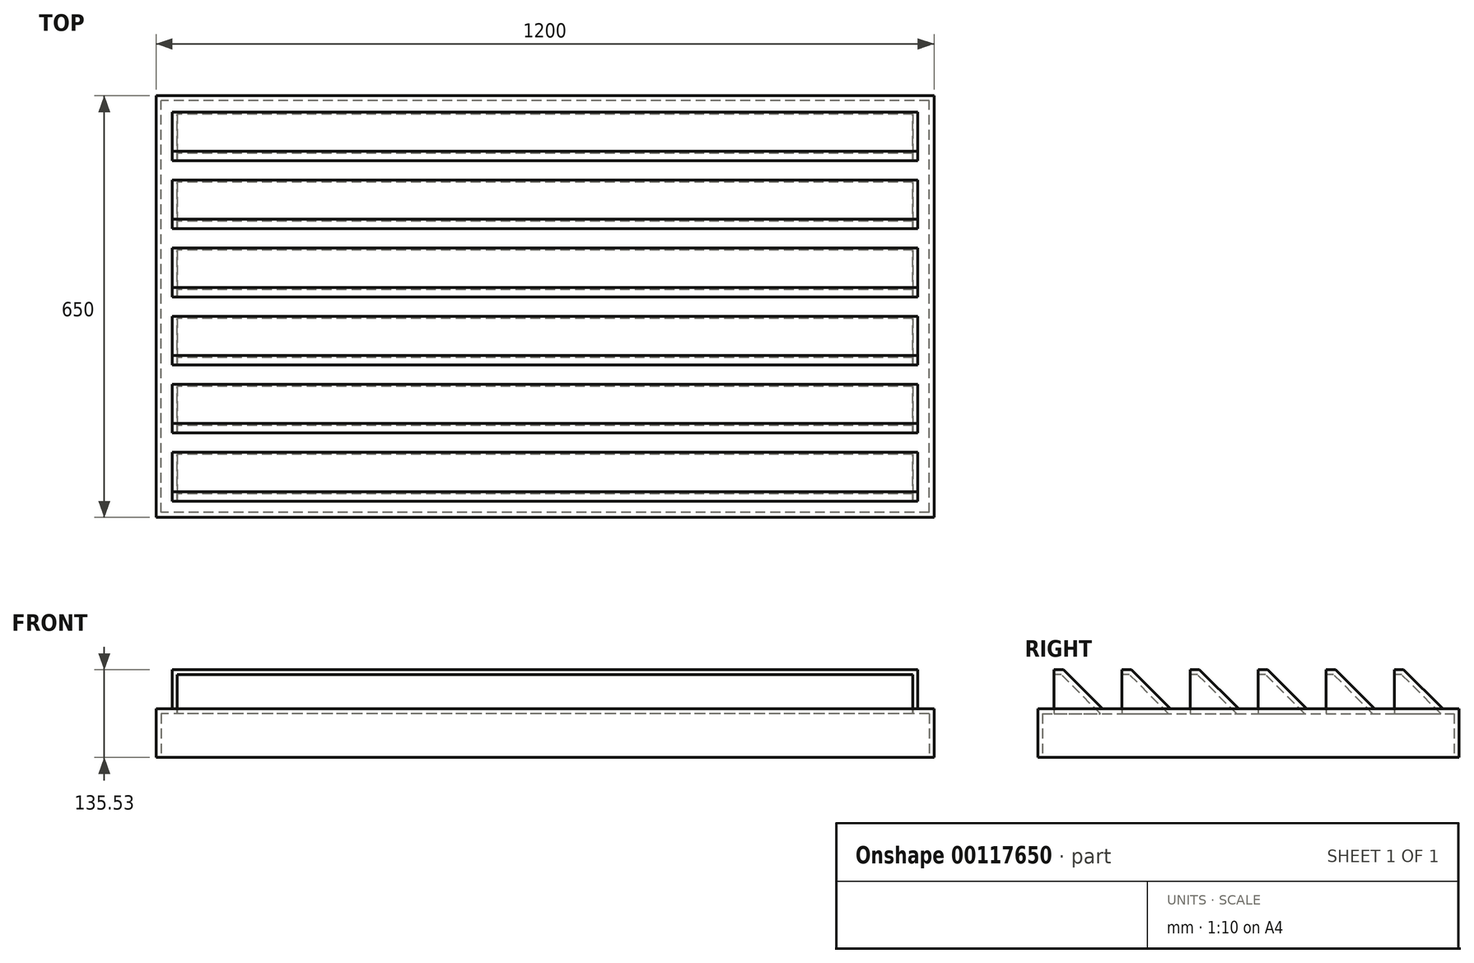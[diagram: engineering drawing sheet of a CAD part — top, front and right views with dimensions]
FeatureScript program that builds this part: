
annotation { "Feature Type Name" : "Feature", "Feature Type Description" : "" }
export const myFeature = defineFeature(function(context is Context, id is Id, definition is map)
    precondition{}
    {
        {
            var Q0;
            Q0=qCreatedBy(makeId("Top.planeOp"),FACE);
            var sketch = newSketch(context, id + "F0", { "sketchPlane" : qUnion([Q0])});
            skLineSegment(sketch, "E0.bottom", {"start": v(600, -325) * mm, "end": v(-600, -325) * mm});
            skLineSegment(sketch, "E0.top", {"start": v(600, 325) * mm, "end": v(-600, 325) * mm});
            skLineSegment(sketch, "E0.left", {"start": v(600, -325) * mm, "end": v(600, 325) * mm});
            skLineSegment(sketch, "E0.right", {"start": v(-600, -325) * mm, "end": v(-600, 325) * mm});
            skPoint(sketch, "E0.middle", {"position": v(0, 0) * mm});
            skSolve(sketch);
        }
        {
            var Q0;
            Q0=makeQuery(id+"F0.imprint","IMPRINT",FACE,{"disambiguationData":[TD([[makeQuery(id+"F0.imprint","IMPRINT",EDGE,{"derivedFrom":sQuery(id+"F0.wireOp",EDGE,"E0.bottom")}),-1.0]])]});
            extrude(context, id + "F1", {"entities" : qUnion([Q0]), "depth" : 75 * mm});
        }
        {
            var Q0;
            Q0=makeQuery(id+"F1.opExtrude","SWEPT_FACE",FACE,{"disambiguationData":[OSD([sQuery(id+"F0.wireOp",EDGE,"E0.right")])]});
            var sketch = newSketch(context, id + "F2", { "sketchPlane" : qUnion([Q0])});
            skLineSegment(sketch, "E1", {"start": v(-300, 75) * mm, "end": v(-225, 150) * mm});
            skLineSegment(sketch, "E2", {"start": v(-225, 150) * mm, "end": v(-225, 75) * mm});
            skLineSegment(sketch, "E3", {"start": v(-239.47, 135.53) * mm, "end": v(360, 135.53) * mm});
            skLineSegment(sketch, "E4.1.0.0", {"start": v(-195, 75) * mm, "end": v(-120, 150) * mm});
            skLineSegment(sketch, "E4.1.0.1", {"start": v(-120, 150) * mm, "end": v(-120, 75) * mm});
            skLineSegment(sketch, "E4.2.0.0", {"start": v(-90, 75) * mm, "end": v(-15, 150) * mm});
            skLineSegment(sketch, "E4.2.0.1", {"start": v(-15, 150) * mm, "end": v(-15, 75) * mm});
            skLineSegment(sketch, "E4.3.0.0", {"start": v(15, 75) * mm, "end": v(90, 150) * mm});
            skLineSegment(sketch, "E4.3.0.1", {"start": v(90, 150) * mm, "end": v(90, 75) * mm});
            skLineSegment(sketch, "E4.4.0.0", {"start": v(120, 75) * mm, "end": v(195, 150) * mm});
            skLineSegment(sketch, "E4.4.0.1", {"start": v(195, 150) * mm, "end": v(195, 75) * mm});
            skLineSegment(sketch, "E4.5.0.0", {"start": v(225, 75) * mm, "end": v(300, 150) * mm});
            skLineSegment(sketch, "E4.5.0.1", {"start": v(300, 150) * mm, "end": v(300, 75) * mm});
            skLineSegment(sketch, "E4.direction1", {"start": v(-300, 75) * mm, "end": v(-195, 75) * mm, "construction": true});
            skSolve(sketch);
        }
        {
            var Q0;
            {var subQ0=sQuery(id+"F2.wireOp",EDGE,"E1");var subQ1=makeQuery(id+"F1.opExtrude","CAP_EDGE",EDGE,{"disambiguationData":[OSD([sQuery(id+"F0.wireOp",EDGE,"E0.right")])],"isStart":false});var subQ2=makeQuery(id+"F2.imprint","INTERSECT",VERTEX,{"derivedFrom":[subQ1,subQ0]});Q0=makeQuery(id+"F2.imprint","IMPRINT",FACE,{"disambiguationData":[TD([[makeQuery(id+"F2.imprint","IMPRINT",EDGE,{"disambiguationData":[TD([[subQ2,-1.0]])],"derivedFrom":subQ0}),-1.0]])]});}
            var Q1;
            {var subQ0=sQuery(id+"F2.wireOp",EDGE,"E4.1.0.0");var subQ1=sQuery(id+"F2.wireOp",EDGE,"E3");var subQ2=makeQuery(id+"F2.imprint","INTERSECT",VERTEX,{"derivedFrom":[subQ1,subQ0]});Q1=makeQuery(id+"F2.imprint","IMPRINT",FACE,{"disambiguationData":[TD([[makeQuery(id+"F2.imprint","IMPRINT",EDGE,{"disambiguationData":[TD([[subQ2,-1.0]])],"derivedFrom":subQ1}),-1.0]])]});}
            var Q2;
            {var subQ0=sQuery(id+"F2.wireOp",EDGE,"E4.2.0.0");var subQ1=sQuery(id+"F2.wireOp",EDGE,"E3");var subQ2=makeQuery(id+"F2.imprint","INTERSECT",VERTEX,{"derivedFrom":[subQ1,subQ0]});Q2=makeQuery(id+"F2.imprint","IMPRINT",FACE,{"disambiguationData":[TD([[makeQuery(id+"F2.imprint","IMPRINT",EDGE,{"disambiguationData":[TD([[subQ2,-1.0]])],"derivedFrom":subQ1}),-1.0]])]});}
            var Q3;
            {var subQ0=sQuery(id+"F2.wireOp",EDGE,"E4.3.0.0");var subQ1=sQuery(id+"F2.wireOp",EDGE,"E3");var subQ2=makeQuery(id+"F2.imprint","INTERSECT",VERTEX,{"derivedFrom":[subQ1,subQ0]});Q3=makeQuery(id+"F2.imprint","IMPRINT",FACE,{"disambiguationData":[TD([[makeQuery(id+"F2.imprint","IMPRINT",EDGE,{"disambiguationData":[TD([[subQ2,-1.0]])],"derivedFrom":subQ1}),-1.0]])]});}
            var Q4;
            {var subQ0=sQuery(id+"F2.wireOp",EDGE,"E4.4.0.0");var subQ1=sQuery(id+"F2.wireOp",EDGE,"E3");var subQ2=makeQuery(id+"F2.imprint","INTERSECT",VERTEX,{"derivedFrom":[subQ1,subQ0]});Q4=makeQuery(id+"F2.imprint","IMPRINT",FACE,{"disambiguationData":[TD([[makeQuery(id+"F2.imprint","IMPRINT",EDGE,{"disambiguationData":[TD([[subQ2,-1.0]])],"derivedFrom":subQ1}),-1.0]])]});}
            var Q5;
            {var subQ0=sQuery(id+"F2.wireOp",EDGE,"E4.5.0.1");var subQ1=sQuery(id+"F2.wireOp",EDGE,"E3");var subQ2=makeQuery(id+"F2.imprint","INTERSECT",VERTEX,{"derivedFrom":[subQ1,subQ0]});Q5=makeQuery(id+"F2.imprint","IMPRINT",FACE,{"disambiguationData":[TD([[makeQuery(id+"F2.imprint","IMPRINT",EDGE,{"disambiguationData":[TD([[subQ2,1.0]])],"derivedFrom":subQ1}),-1.0]])]});}
            extrude(context, id + "F3", {"entities" : qUnion([Q0, Q1, Q2, Q3, Q4, Q5]), "operationType" : NewBodyOperationType.ADD, "oppositeDirection" : true, "depth" : 1175 * mm, "hasSecondDirection" : true, "secondDirectionOppositeDirection" : true, "secondDirectionDepth" : 25 * mm});
        }
        {
            var Q0;
            Q0=makeQuery(id+"F3.opExtrude","SWEPT_FACE",FACE,{"disambiguationData":[OSD([sQuery(id+"F2.wireOp",EDGE,"E2")])]});
            var Q1;
            Q1=makeQuery(id+"F3.opExtrude","SWEPT_FACE",FACE,{"disambiguationData":[OSD([sQuery(id+"F2.wireOp",EDGE,"475c7ac5-b6c0-4911-8d2d-dd895b44ecf6.1.0.1")])]});
            var Q2;
            Q2=makeQuery(id+"F3.opExtrude","SWEPT_FACE",FACE,{"disambiguationData":[OSD([sQuery(id+"F2.wireOp",EDGE,"475c7ac5-b6c0-4911-8d2d-dd895b44ecf6.2.0.1")])]});
            var Q3;
            Q3=makeQuery(id+"F3.opExtrude","SWEPT_FACE",FACE,{"disambiguationData":[OSD([sQuery(id+"F2.wireOp",EDGE,"475c7ac5-b6c0-4911-8d2d-dd895b44ecf6.3.0.1")])]});
            var Q4;
            Q4=makeQuery(id+"F3.opExtrude","SWEPT_FACE",FACE,{"disambiguationData":[OSD([sQuery(id+"F2.wireOp",EDGE,"475c7ac5-b6c0-4911-8d2d-dd895b44ecf6.4.0.1")])]});
            var Q5;
            Q5=makeQuery(id+"F3.opExtrude","SWEPT_FACE",FACE,{"disambiguationData":[OSD([sQuery(id+"F2.wireOp",EDGE,"475c7ac5-b6c0-4911-8d2d-dd895b44ecf6.5.0.1")])]});
            var Q6;
            Q6=makeQuery(id+"F3.opExtrude","SWEPT_FACE",FACE,{"disambiguationData":[OSD([sQuery(id+"F2.wireOp",EDGE,"475c7ac5-b6c0-4911-8d2d-dd895b44ecf6.6.0.1")])]});
            var Q7;
            Q7=makeQuery(id+"F3.opExtrude","SWEPT_FACE",FACE,{"disambiguationData":[OSD([sQuery(id+"F2.wireOp",EDGE,"475c7ac5-b6c0-4911-8d2d-dd895b44ecf6.7.0.1")])]});
            var Q8;
            Q8=makeQuery(id+"F3.opExtrude","SWEPT_FACE",FACE,{"disambiguationData":[OSD([sQuery(id+"F2.wireOp",EDGE,"475c7ac5-b6c0-4911-8d2d-dd895b44ecf6.8.0.1")])]});
            var Q9;
            Q9=makeQuery(id+"F3.opExtrude","SWEPT_FACE",FACE,{"disambiguationData":[OSD([sQuery(id+"F2.wireOp",EDGE,"475c7ac5-b6c0-4911-8d2d-dd895b44ecf6.9.0.1")])]});
            var Q10;
            Q10=makeQuery(id+"F1.opExtrude","CAP_FACE",FACE,{"disambiguationData":[OSD([sQuery(id+"F0.wireOp",EDGE,"E0.bottom"),sQuery(id+"F0.wireOp",EDGE,"E0.top"),sQuery(id+"F0.wireOp",EDGE,"E0.left"),sQuery(id+"F0.wireOp",EDGE,"E0.right")])],"isStart":true});
            var Q11;
            Q11=makeQuery(id+"F3.opExtrude","SWEPT_FACE",FACE,{"disambiguationData":[OSD([sQuery(id+"F2.wireOp",EDGE,"E4.1.0.1")])]});
            var Q12;
            Q12=makeQuery(id+"F3.opExtrude","SWEPT_FACE",FACE,{"disambiguationData":[OSD([sQuery(id+"F2.wireOp",EDGE,"E4.2.0.1")])]});
            var Q13;
            Q13=makeQuery(id+"F3.opExtrude","SWEPT_FACE",FACE,{"disambiguationData":[OSD([sQuery(id+"F2.wireOp",EDGE,"E4.3.0.1")])]});
            var Q14;
            Q14=makeQuery(id+"F3.opExtrude","SWEPT_FACE",FACE,{"disambiguationData":[OSD([sQuery(id+"F2.wireOp",EDGE,"E4.4.0.1")])]});
            var Q15;
            Q15=makeQuery(id+"F3.opExtrude","SWEPT_FACE",FACE,{"disambiguationData":[OSD([sQuery(id+"F2.wireOp",EDGE,"E4.5.0.1")])]});
            var Q16;
            Q16=makeQuery(id+"F3.opExtrude","SWEPT_FACE",FACE,{"disambiguationData":[OSD([sQuery(id+"F2.wireOp",EDGE,"E4.6.0.1")])]});
            var Q17;
            Q17=makeQuery(id+"F3.opExtrude","SWEPT_FACE",FACE,{"disambiguationData":[OSD([sQuery(id+"F2.wireOp",EDGE,"E4.7.0.1")])]});
            var Q18;
            Q18=makeQuery(id+"F3.opExtrude","SWEPT_FACE",FACE,{"disambiguationData":[OSD([sQuery(id+"F2.wireOp",EDGE,"E4.8.0.1")])]});
            shell(context, id + "F4", {"entities" : qUnion([Q0, Q1, Q2, Q3, Q4, Q5, Q6, Q7, Q8, Q9, Q10, Q11, Q12, Q13, Q14, Q15, Q16, Q17, Q18]), "thickness" : 7.5 * mm});
        }
    });
